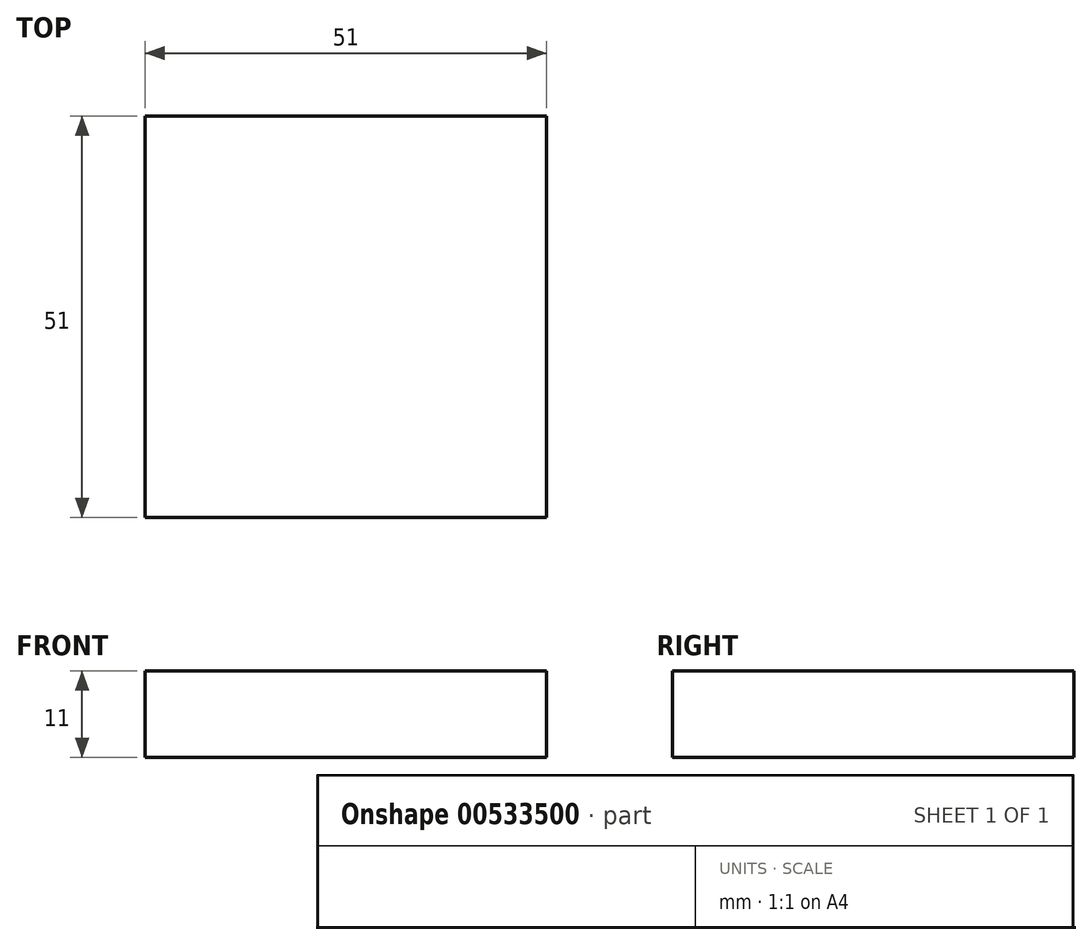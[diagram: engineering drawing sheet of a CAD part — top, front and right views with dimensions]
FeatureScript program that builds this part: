
annotation { "Feature Type Name" : "Feature", "Feature Type Description" : "" }
export const myFeature = defineFeature(function(context is Context, id is Id, definition is map)
    precondition{}
    {
        {
            var Q0;
            Q0=qCreatedBy(makeId("Top.planeOp"),FACE);
            var sketch = newSketch(context, id + "F0", { "sketchPlane" : qUnion([Q0])});
            skLineSegment(sketch, "E0.bottom", {"start": v(0, 0) * mm, "end": v(51, 0) * mm});
            skLineSegment(sketch, "E0.top", {"start": v(0, 51) * mm, "end": v(51, 51) * mm});
            skLineSegment(sketch, "E0.left", {"start": v(0, 0) * mm, "end": v(0, 51) * mm});
            skLineSegment(sketch, "E0.right", {"start": v(51, 0) * mm, "end": v(51, 51) * mm});
            skSolve(sketch);
        }
        {
            var Q0;
            Q0=qSketchRegion(id+"F0",true);
            extrude(context, id + "F1", {"entities" : qUnion([Q0]), "depth" : 11 * mm, "offsetDistance" : 25 * mm});
        }
    });
